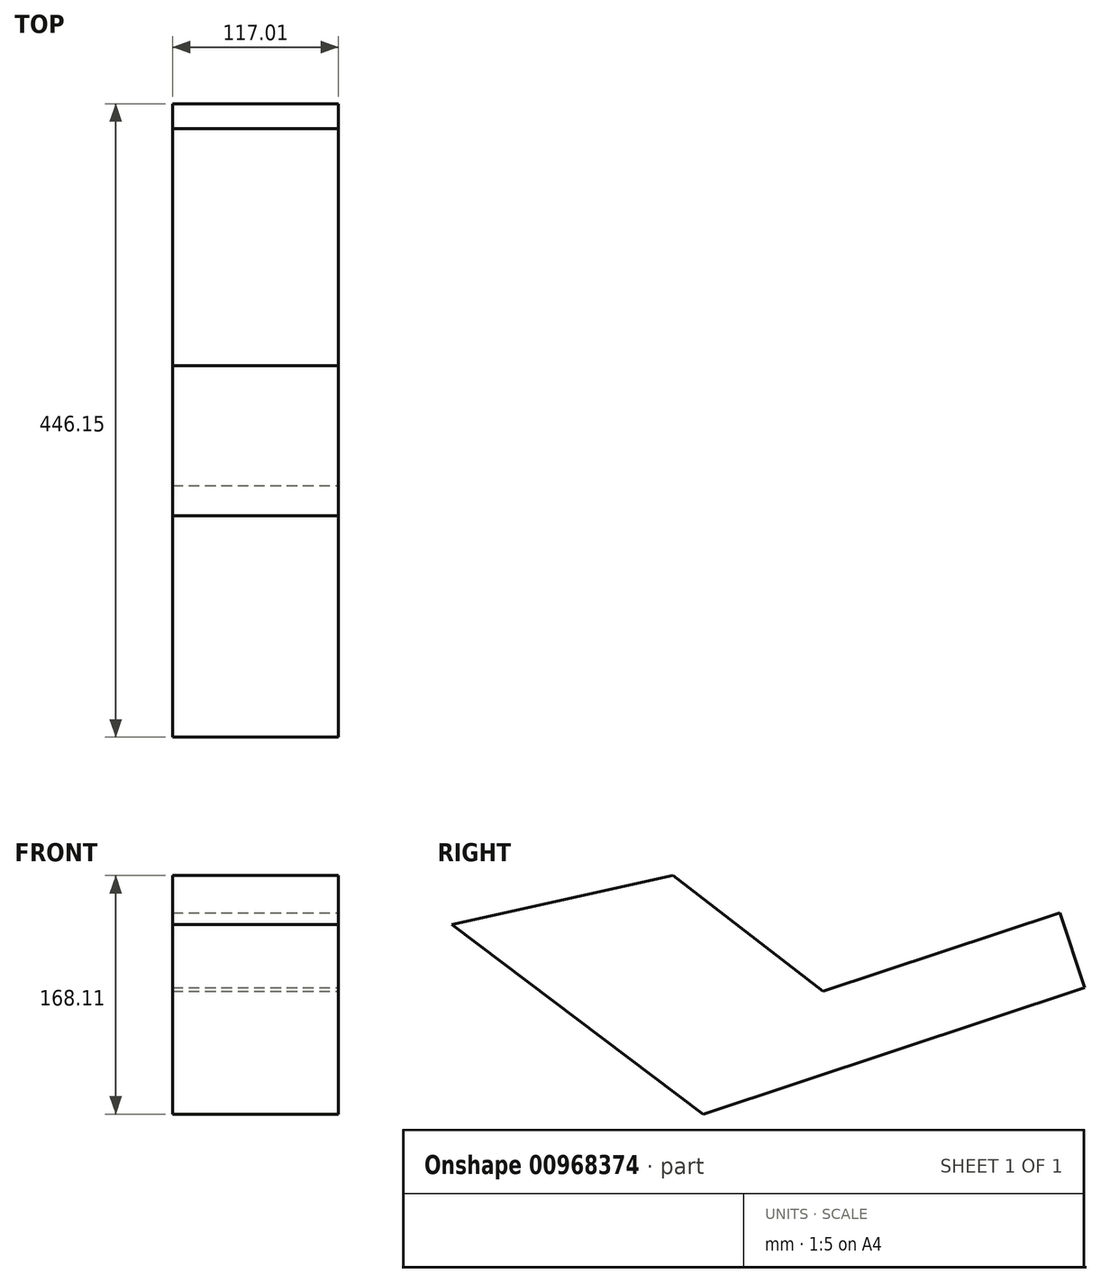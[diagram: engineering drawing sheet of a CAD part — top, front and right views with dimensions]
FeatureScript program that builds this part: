
annotation { "Feature Type Name" : "Feature", "Feature Type Description" : "" }
export const myFeature = defineFeature(function(context is Context, id is Id, definition is map)
    precondition{}
    {
        {
            var Q0;
            Q0=qCreatedBy(makeId("Right.planeOp"),FACE);
            var sketch = newSketch(context, id + "F0", { "sketchPlane" : qUnion([Q0])});
            skLineSegment(sketch, "E0", {"start": v(-49.26, 32.76) * mm, "end": v(106.64, 67.47) * mm});
            skLineSegment(sketch, "E1", {"start": v(106.64, 67.47) * mm, "end": v(212.36, -14.2) * mm});
            skLineSegment(sketch, "E2", {"start": v(212.36, -14.2) * mm, "end": v(229.8, -66.94) * mm});
            skLineSegment(sketch, "E3", {"start": v(229.8, -66.94) * mm, "end": v(127.89, -100.64) * mm});
            skLineSegment(sketch, "E4", {"start": v(127.89, -100.64) * mm, "end": v(-49.26, 32.76) * mm});
            skSolve(sketch);
        }
        {
            var Q0;
            Q0 = qSketchRegion(id + "F0", true);
            extrude(context, id + "F1", {"entities" : qUnion([Q0]), "oppositeDirection" : true, "depth" : 117 * mm, "offsetDistance" : 25.4 * mm});
        }
        {
            var Q0;
            Q0=makeQuery(id+"F1.opExtrude","SWEPT_FACE",FACE,{"disambiguationData":[OSD([sQuery(id+"F0.wireOp",EDGE,"E2")])]});
            extrude(context, id + "F2", {"entities" : qUnion([Q0]), "operationType" : NewBodyOperationType.ADD, "depth" : 176 * mm, "offsetDistance" : 25.4 * mm});
        }
    });
